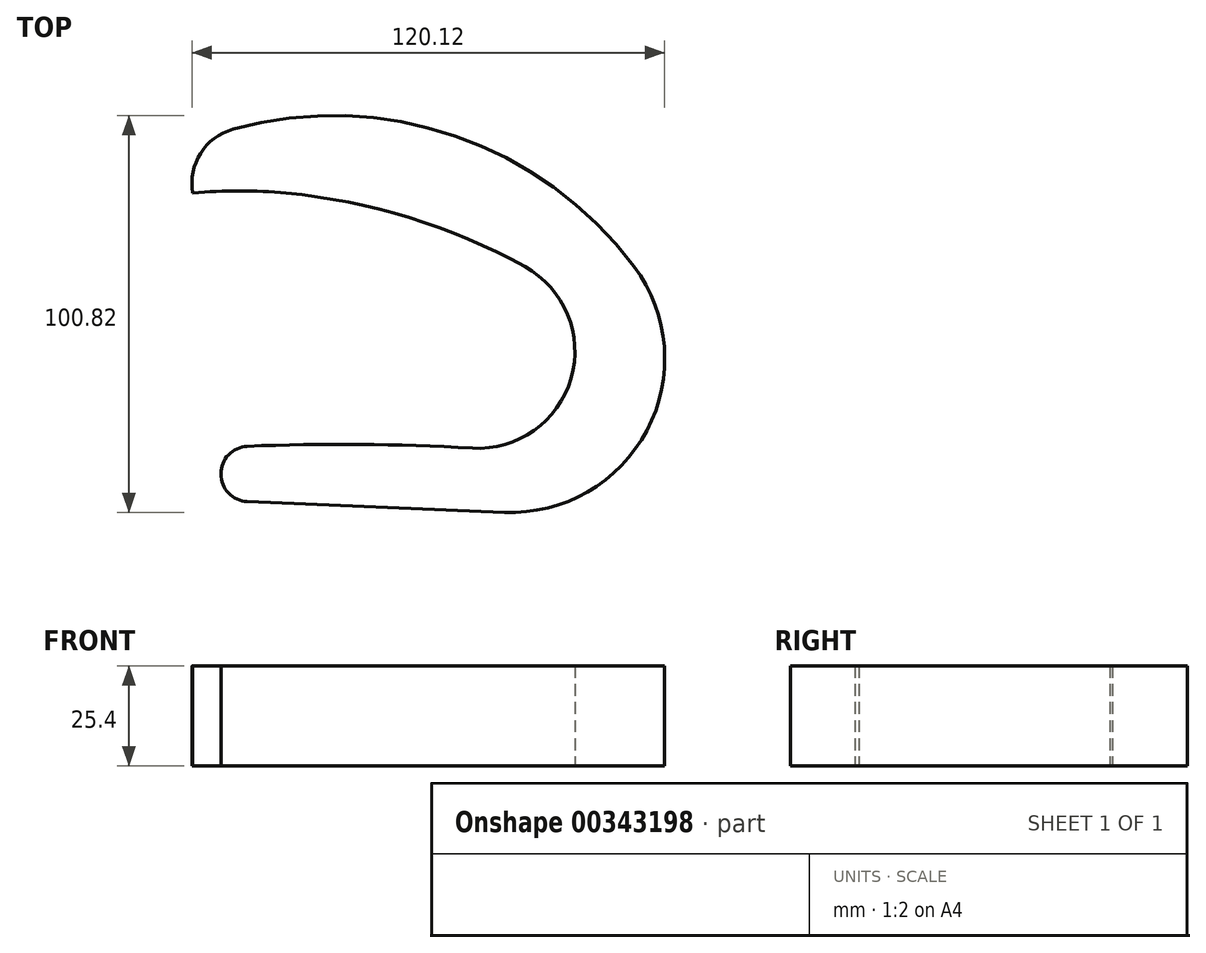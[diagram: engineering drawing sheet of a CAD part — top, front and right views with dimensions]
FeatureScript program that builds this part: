
annotation { "Feature Type Name" : "Feature", "Feature Type Description" : "" }
export const myFeature = defineFeature(function(context is Context, id is Id, definition is map)
    precondition{}
    {
        {
            var Q0;
            Q0=qCreatedBy(makeId("Top.planeOp"),FACE);
            var sketch = newSketch(context, id + "F0", { "sketchPlane" : qUnion([Q0])});
            skLineSegment(sketch, "E0", {"start": v(-70.5, -20.57) * mm, "end": v(-5.17, -23.3) * mm});
            skArc(sketch, "E1", {"start": v(-5.17, -23.3) * mm, "mid": v(31.01, -2.51) * mm, "end": v(27.8, 39.1) * mm});
            skArc(sketch, "E2", {"start": v(27.8, 39.1) * mm, "mid": v(-17.77, 72.33) * mm, "end": v(-74.15, 74.03) * mm});
            skArc(sketch, "E3", {"start": v(-70.5, -20.57) * mm, "mid": v(-77.23, -13.55) * mm, "end": v(-70.5, -6.53) * mm});
            skArc(sketch, "E4", {"start": v(-70.5, -6.53) * mm, "mid": v(-41.91, -6.06) * mm, "end": v(-13.34, -7.01) * mm});
            skArc(sketch, "E5", {"start": v(-13.34, -7.01) * mm, "mid": v(11.75, 10.71) * mm, "end": v(0, 39.1) * mm});
            skArc(sketch, "E6", {"start": v(0, 39.1) * mm, "mid": v(-29.35, 51.57) * mm, "end": v(-60.62, 57.8) * mm});
            skArc(sketch, "E7", {"start": v(-60.62, 57.8) * mm, "mid": v(-72.49, 58.36) * mm, "end": v(-84.36, 57.8) * mm});
            skArc(sketch, "E8", {"start": v(-74.15, 74.03) * mm, "mid": v(-82.4, 67.9) * mm, "end": v(-84.36, 57.8) * mm});
            skSolve(sketch);
        }
        {
            var Q0;
            Q0 = qSketchRegion(id + "F0", true);
            extrude(context, id + "F1", {"entities" : qUnion([Q0]), "depth" : 25.4 * mm});
        }
    });
